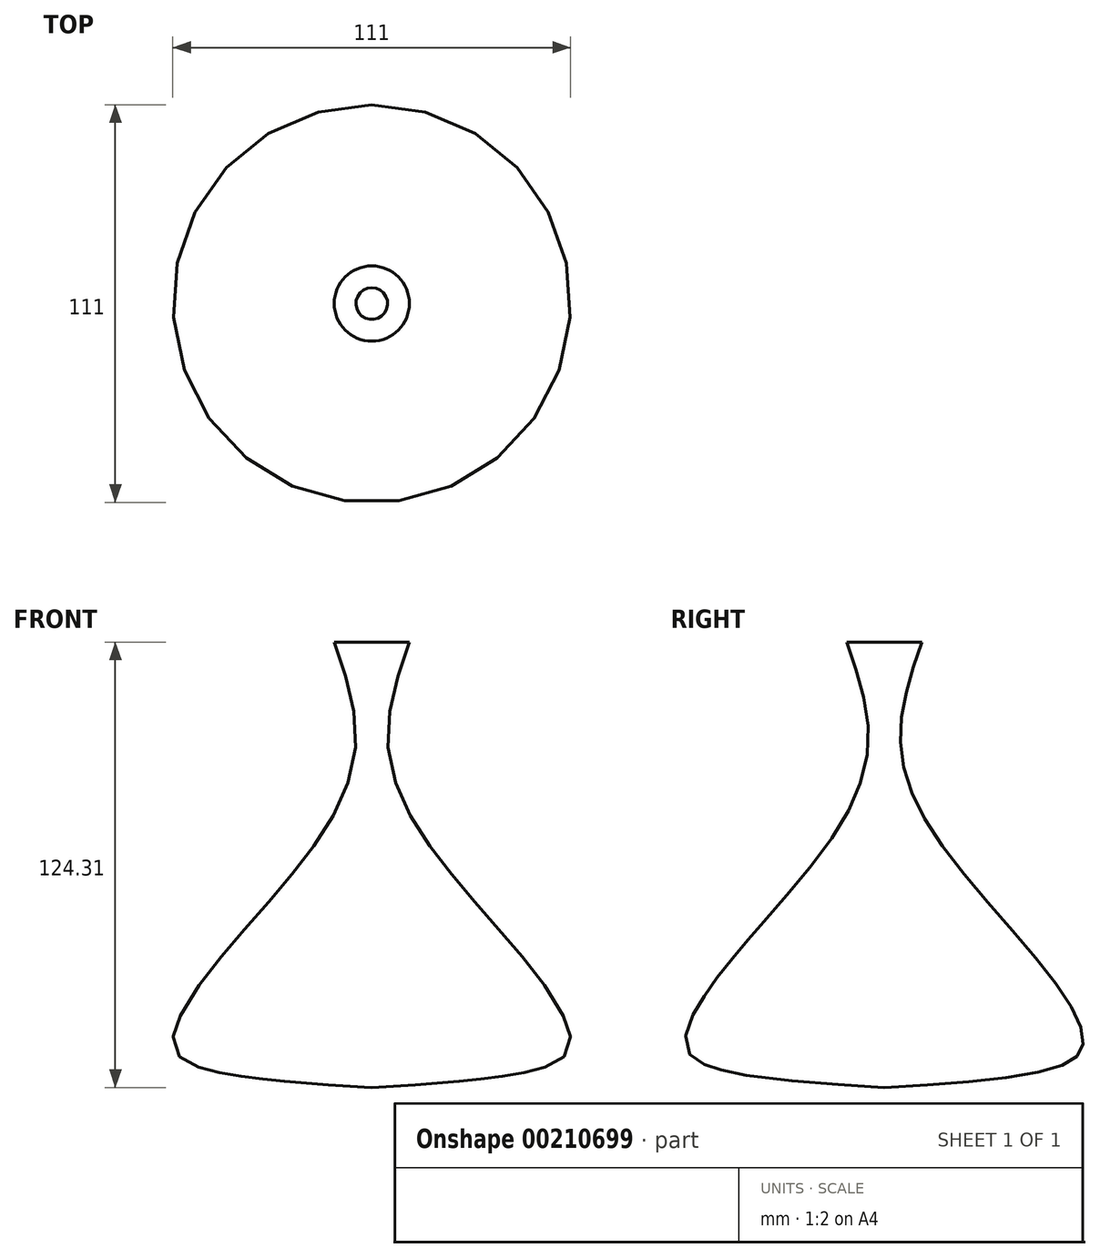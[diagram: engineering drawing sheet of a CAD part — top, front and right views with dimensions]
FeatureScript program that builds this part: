
annotation { "Feature Type Name" : "Feature", "Feature Type Description" : "" }
export const myFeature = defineFeature(function(context is Context, id is Id, definition is map)
    precondition{}
    {
        {
            var Q0;
            Q0=qCreatedBy(makeId("Right.planeOp"),FACE);
            var sketch = newSketch(context, id + "F0", { "sketchPlane" : qUnion([Q0])});
            skFitSpline(sketch, "E0", {"points": [v(10.5, 54.79) * mm, v(4.44, 29.36) * mm, v(13.32, 2.12) * mm, v(45.2, -37.03) * mm, v(55.5, -56.8) * mm, v(49.84, -63.26) * mm, v(0, -69.52) * mm], "startDerivative": vector(-55.73, -161.02) * mm, "endDerivative": vector(-278.97, -16.98) * mm});
            skLineSegment(sketch, "E1", {"start": v(0, 72.95) * mm, "end": v(0, 59.43) * mm});
            skSolve(sketch);
        }
        {
            var Q0;
            Q0=sQuery(id+"F0.wireOp",EDGE,"E0");
            var Q1;
            Q1=sQuery(id+"F0.wireOp",EDGE,"E1");
            revolve(context, id + "F1", {"bodyType" : ToolBodyType.SURFACE, "surfaceEntities" : qUnion([Q0]), "axis" : qUnion([Q1]), "revolveType" : RevolveType.FULL});
        }
    });
